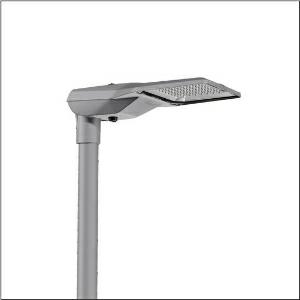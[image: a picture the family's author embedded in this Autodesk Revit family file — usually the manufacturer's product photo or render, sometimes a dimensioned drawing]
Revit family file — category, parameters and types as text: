
# Revit family: streetlight_sl_21_midi___st1_0a_5xe3d33t08nb_d416
name_source: partatom
category: Lighting Fixtures
units: mm (PartAtom-declared; Revit-internal decimal feet)

## family parameters
Cut with Voids When Loaded = No
Host = Face
Light Source = No
Part Type = Normal
Room Calculation Point = No
Round Connector Dimension = Use Diameter
Shared = No

## types (1)
- --- (1 x LED, 22700 lm, 151.2 W, 3000K)
    Apparent Load = 151 VA
    CIE Flux Codes = 40 73 97 100 100
    Color Rendering = 70
    Color Temperature = 3000K
    Default Elevation = 1800 mm
    Description = Streetlight SL 21 midi, mast luminaire, primary light control with lens, of PMMA, primary optical cover: cover, of toughened safety glass, transparent, light distribution: ST1.0a, light emission: direct distribution, primary light characteristic: asymmetric, installation type: side-entry, post-top, LED, High Power LED, rated luminous flux: 22.700lm, luminous efficacy: 150lm/W, light colour: 730, colour temperature: 3000K, control gear: D4i, control: flexible luminous flux parameterisation, time-dependent luminous flux control, constant luminous flux control, overheat protection, pre-setting: logarithmic dimming characteristic, mains connection: 230..240V, AC, 50/60Hz, start of lifetime: 151W, end of service life: 157W, reduction: 70W, luminaire housing, of diecast aluminium, powder-coated, Siteco® metallic grey (DB 702S), corrosivity category C5 mid according to DIN EN ISO 12944, please order mast flange separately, inclination adjustable: 0°, 5°, 10°, 15°, sealing non-destructively replaceable, multi-level sealing system, length: 644mm, width: 335mm, height: 110mm, mast flange for spigot size: 42mm (side-entry): 5XC10008XM4, 60/48mm (side-entry/post-top): 5XC10108XM2, 76/60mm (side-entry/post-top): 5XC10108XM1, mounting height: 4..8m, Smart Interface below and above, protection rating (complete): IP66, insulation class (complete): insulation class II (safety insulation), certification: CE, ENEC, ENEC+, VDE, impact resistance: IK10, permissible operating ambient temperature for outdoor applications: -40..+50°C, standard-compliant lighting for roads and squares, packaging unit: 1 piece

Light Distribution: ST1.0a
    Height = 111 mm
    Lamp = 1 x LED
    Lamp Light Flux = 22700 lm
    Lamp Power = 151.2 W
    Lamp count = 1
    Length = 644 mm
    Luminous efficacy = 150 lm/W
    Manufacturer = Siteco
    ModVariant = No
    Model = 5XE3D33T08NB
    Number of Poles = 1
    OnlyDefault = Yes
    Power Factor = 1
    Product Name = Streetlight SL 21 midi | ST1.0a
    Product group = mast luminaire | pylon top
    ProductGroupID = 6100
    Protection Class = Protection class II
    Protection Degree = IP 66
    RLX_Detail_Level = 1
    RLX_Emergency_Light_Flux = 0 lm
    RLX_Emergency_Type = 0
    RLX_Emergency_Type_DB = No
    RlxData = <blob elided: 27105 chars, md5=34656a65>
    Socket = socket
    Standby Power = 0 W
    System Light Flux = 22700 lm
    System Power = 151 W
    Type Comments = factory setting: luminous flux: 100 % | dim-lin: 254 | 802 mA
    Type Image = l_1004304.jpg
    URL = http://relux.com
    VarID = @adj_170500
    Voltage = 0 V
    Weight = 0.00 kg
    Width = 336 mm

## geometry (parser evidence)
native form markers: Blend x4, Sweep x12
no freeform markers — native parametric forms only
